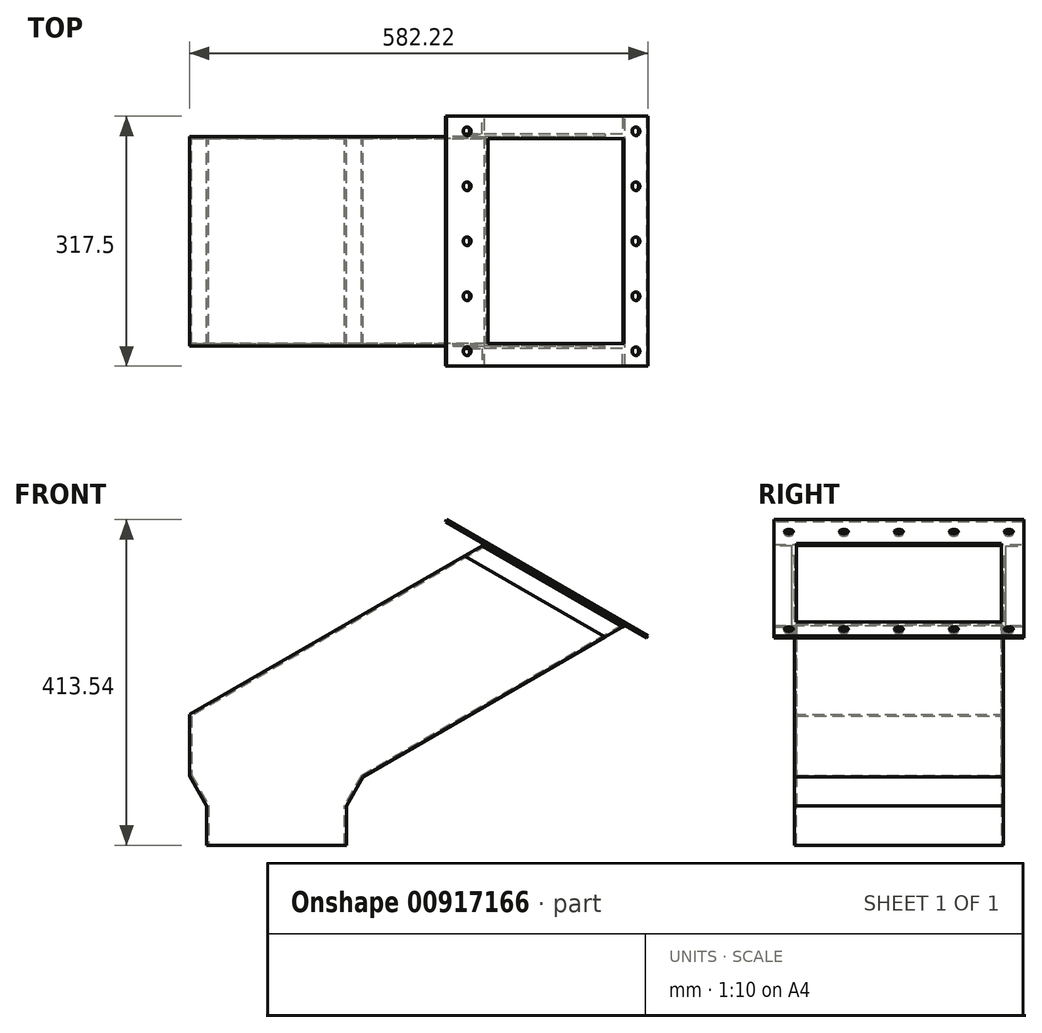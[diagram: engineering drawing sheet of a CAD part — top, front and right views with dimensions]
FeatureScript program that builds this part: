
annotation { "Feature Type Name" : "Feature", "Feature Type Description" : "" }
export const myFeature = defineFeature(function(context is Context, id is Id, definition is map)
    precondition{}
    {
        {
            var Q0;
            Q0=qCreatedBy(makeId("Front.planeOp"),FACE);
            var sketch = newSketch(context, id + "F0", { "sketchPlane" : qUnion([Q0])});
            skLineSegment(sketch, "E0", {"start": v(-317.85, 2733.04) * mm, "end": v(355.25, 2344.43) * mm});
            skLineSegment(sketch, "E1", {"start": v(355.25, 2344.43) * mm, "end": v(1028.35, 2733.04) * mm});
            skLineSegment(sketch, "E2", {"start": v(-317.85, 2733.04) * mm, "end": v(-317.85, 4597.4) * mm});
            skLineSegment(sketch, "E3", {"start": v(-317.85, 4597.4) * mm, "end": v(1028.35, 4597.4) * mm});
            skLineSegment(sketch, "E4", {"start": v(1028.35, 2733.04) * mm, "end": v(1028.35, 4597.4) * mm});
            skLineSegment(sketch, "E5", {"start": v(-317.85, 2733.04) * mm, "end": v(1028.35, 2733.04) * mm, "construction": true});
            skLineSegment(sketch, "E6", {"start": v(-317.85, 2739.4) * mm, "end": v(-368.65, 2739.4) * mm});
            skLineSegment(sketch, "E7", {"start": v(-368.65, 2733.04) * mm, "end": v(-368.65, 2739.4) * mm});
            skLineSegment(sketch, "E8", {"start": v(-368.65, 2733.04) * mm, "end": v(1079.15, 2733.04) * mm});
            skLineSegment(sketch, "E9", {"start": v(1079.15, 2739.4) * mm, "end": v(1079.15, 2733.04) * mm});
            skLineSegment(sketch, "E10", {"start": v(1079.15, 2739.4) * mm, "end": v(1028.35, 2739.4) * mm});
            skLineSegment(sketch, "E11", {"start": v(355.25, 4597.4) * mm, "end": v(355.25, 2344.43) * mm, "construction": true});
            skLineSegment(sketch, "E12", {"start": v(355.25, 2344.43) * mm, "end": v(0, 2139.33) * mm, "construction": true});
            skLineSegment(sketch, "E13", {"start": v(0, 2088) * mm, "end": v(0, 0) * mm, "construction": true});
            skLineSegment(sketch, "E14", {"start": v(-1118.25, 0) * mm, "end": v(0, 0) * mm, "construction": true});
            skLineSegment(sketch, "E15", {"start": v(-317.85, 2739.4) * mm, "end": v(-317.85, 2088) * mm, "construction": true});
            skLineSegment(sketch, "E16", {"start": v(-317.85, 2088) * mm, "end": v(-88.9, 2088) * mm, "construction": true});
            skLineSegment(sketch, "E17", {"start": v(-88.9, 2088) * mm, "end": v(0, 2088) * mm, "construction": true});
            skLineSegment(sketch, "E18", {"start": v(0, 2088) * mm, "end": v(0, 2139.33) * mm, "construction": true});
            skLineSegment(sketch, "E19", {"start": v(0, 2088) * mm, "end": v(0, 2088) * mm});
            skSolve(sketch);
        }
        {
            var Q0;
            Q0=qCreatedBy(makeId("Right.planeOp"),FACE);
            var sketch = newSketch(context, id + "F1", { "sketchPlane" : qUnion([Q0])});
            skLineSegment(sketch, "E20", {"start": v(0, 2549.53) * mm, "end": v(-535.95, 2549.53) * mm});
            skSolve(sketch);
        }
        {
            var Q0;
            Q0=sQuery(id+"F1.wireOp",VERTEX,"E20.end");
            var Q1;
            Q1=sQuery(id+"F0.wireOp",VERTEX,"E0.start");
            var Q2;
            Q2=sQuery(id+"F0.wireOp",VERTEX,"E0.end");
            cPlane(context, id + "F2", {"entities" : qUnion([Q0, Q1, Q2]), "cplaneType" : CPlaneType.THREE_POINT, "offset" : 3.17 * mm, "oppositeDirection" : true, "width" : 152.4 * mm, "height" : 152.4 * mm});
        }
        {
            var Q0;
            Q0=qCreatedBy(id+"F2.planeOp",FACE);
            var sketch = newSketch(context, id + "F3", { "sketchPlane" : qUnion([Q0])});
            skLineSegment(sketch, "E21.bottom", {"start": v(-1067.66, -130.18) * mm, "end": v(-1067.66, 130.17) * mm});
            skLineSegment(sketch, "E21.top", {"start": v(-867.64, -130.18) * mm, "end": v(-867.64, 130.17) * mm});
            skLineSegment(sketch, "E21.left", {"start": v(-1067.66, 130.17) * mm, "end": v(-867.64, 130.17) * mm});
            skLineSegment(sketch, "E21.right", {"start": v(-1067.66, -130.18) * mm, "end": v(-867.64, -130.18) * mm});
            skLineSegment(sketch, "E22.bottom", {"start": v(-1127.99, 158.75) * mm, "end": v(-832.71, 158.75) * mm});
            skLineSegment(sketch, "E22.top", {"start": v(-1127.99, -158.75) * mm, "end": v(-832.71, -158.75) * mm});
            skLineSegment(sketch, "E22.left", {"start": v(-1127.99, 158.75) * mm, "end": v(-1127.99, -158.75) * mm});
            skLineSegment(sketch, "E22.right", {"start": v(-832.71, 158.75) * mm, "end": v(-832.71, -158.75) * mm});
            skLineSegment(sketch, "E23", {"start": v(-967.65, 130.17) * mm, "end": v(-967.65, 158.75) * mm, "construction": true});
            skLineSegment(sketch, "E24", {"start": v(-832.71, 0) * mm, "end": v(-867.64, 0) * mm, "construction": true});
            skSolve(sketch);
        }
        {
            var Q0;
            Q0=qSketchRegion(id+"F3",true);
            extrude(context, id + "F4", {"entities" : qUnion([Q0]), "oppositeDirection" : true, "depth" : 3.17 * mm, "offsetDistance" : 25.4 * mm});
        }
        {
            var Q0;
            Q0=qCreatedBy(makeId("Front.planeOp"),FACE);
            var sketch = newSketch(context, id + "F5", { "sketchPlane" : qUnion([Q0])});
            skLineSegment(sketch, "E25", {"start": v(-175.13, 2062.6) * mm, "end": v(-2.67, 2062.6) * mm});
            skLineSegment(sketch, "E26", {"start": v(-2.67, 2062.6) * mm, "end": v(-2.67, 2113.4) * mm});
            skLineSegment(sketch, "E27", {"start": v(18.93, 2151.5) * mm, "end": v(-2.67, 2113.4) * mm});
            skLineSegment(sketch, "E28", {"start": v(18.93, 2151.5) * mm, "end": v(351, 2343.22) * mm});
            skLineSegment(sketch, "E29", {"start": v(351, 2343.22) * mm, "end": v(177.77, 2443.23) * mm});
            skLineSegment(sketch, "E30", {"start": v(177.77, 2443.23) * mm, "end": v(-196.73, 2227.02) * mm});
            skLineSegment(sketch, "E31", {"start": v(-196.73, 2227.02) * mm, "end": v(-196.73, 2151.5) * mm});
            skLineSegment(sketch, "E32", {"start": v(-196.73, 2151.5) * mm, "end": v(-175.13, 2113.4) * mm});
            skLineSegment(sketch, "E33", {"start": v(-175.13, 2113.4) * mm, "end": v(-175.13, 2062.6) * mm});
            skLineSegment(sketch, "E34", {"start": v(-88.9, 2062.6) * mm, "end": v(-88.9, 2189.26) * mm, "construction": true});
            skPoint(sketch, "E34.endSnap0", {"position": v(351, 2343.22) * mm});
            skLineSegment(sketch, "E35", {"start": v(-88.9, 2189.26) * mm, "end": v(264.38, 2393.23) * mm, "construction": true});
            skLineSegment(sketch, "E36", {"start": v(-88.9, 2088) * mm, "end": v(-88.9, 2062.6) * mm, "construction": true});
            skSolve(sketch);
        }
        {
            var Q0;
            Q0=qSketchRegion(id+"F5",true);
            extrude(context, id + "F6", {"entities" : qUnion([Q0]), "endBound" : BoundingType.SYMMETRIC, "depth" : 260.35 * mm, "offsetDistance" : 25.4 * mm});
        }
        {
            var Q0;
            Q0=makeQuery(id+"F6.opExtrude","SWEPT_FACE",FACE,{"disambiguationData":[OSD([sQuery(id+"F5.wireOp",EDGE,"E29")])]});
            var Q1;
            Q1=makeQuery(id+"F6.opExtrude","SWEPT_FACE",FACE,{"disambiguationData":[OSD([sQuery(id+"F5.wireOp",EDGE,"E25")])]});
            shell(context, id + "F7", {"entities" : qUnion([Q0, Q1]), "thickness" : 2.67 * mm, "oppositeDirection" : true});
        }
        {
            var Q0;
            Q0=sQuery(id+"F0.wireOp",VERTEX,"E0.end");
            var Q1;
            Q1=qCreatedBy(makeId("Right.planeOp"),FACE);
            cPlane(context, id + "F8", {"entities" : qUnion([Q0, Q1]), "cplaneType" : CPlaneType.PLANE_POINT, "offset" : 25.4 * mm, "width" : 152.4 * mm, "height" : 152.4 * mm});
        }
        {
            var Q0;
            Q0=qCreatedBy(id+"F8.planeOp",FACE);
            var sketch = newSketch(context, id + "F9", { "sketchPlane" : qUnion([Q0])});
            skLineSegment(sketch, "E37", {"start": v(0, 2344.43) * mm, "end": v(-111.8, 2344.43) * mm});
            skSolve(sketch);
        }
        {
            var Q0;
            Q0=sQuery(id+"F9.wireOp",EDGE,"E37");
            cPlane(context, id + "F10", {"entities" : qUnion([Q0]), "cplaneType" : CPlaneType.LINE_ANGLE, "offset" : 25.4 * mm, "angle" : 60 * degree, "width" : 152.4 * mm, "height" : 152.4 * mm});
        }
        {
            var Q0;
            Q0=qCreatedBy(id+"F10.planeOp",FACE);
            var Q1;
            Q1=sQuery(id+"F5.wireOp",VERTEX,"E35.end");
            cPlane(context, id + "F11", {"entities" : qUnion([Q0, Q1]), "cplaneType" : CPlaneType.PLANE_POINT, "offset" : 25.4 * mm, "width" : 152.4 * mm, "height" : 152.4 * mm});
        }
        {
            var Q0;
            Q0=qCreatedBy(id+"F11.planeOp",FACE);
            var sketch = newSketch(context, id + "F12", { "sketchPlane" : qUnion([Q0])});
            skLineSegment(sketch, "E38", {"start": v(-132.84, 2204.79) * mm, "end": v(-132.84, 2179.39) * mm});
            skLineSegment(sketch, "E39", {"start": v(-132.84, 2179.39) * mm, "end": v(-136.02, 2179.39) * mm});
            skLineSegment(sketch, "E40", {"start": v(-136.02, 2179.39) * mm, "end": v(-136.02, 2201.61) * mm});
            skLineSegment(sketch, "E41", {"start": v(-136.02, 2201.61) * mm, "end": v(-158.24, 2201.61) * mm});
            skLineSegment(sketch, "E42", {"start": v(-158.24, 2201.61) * mm, "end": v(-158.24, 2204.79) * mm});
            skLineSegment(sketch, "E43", {"start": v(-158.24, 2204.79) * mm, "end": v(-132.84, 2204.79) * mm});
            skLineSegment(sketch, "E44", {"start": v(0, 2204.79) * mm, "end": v(0, 2243.29) * mm, "construction": true});
            skLineSegment(sketch, "E45.MirrorCS", {"start": v(158.24, 2201.61) * mm, "end": v(158.24, 2204.79) * mm});
            skLineSegment(sketch, "E46.MirrorCS", {"start": v(132.84, 2179.39) * mm, "end": v(136.02, 2179.39) * mm});
            skLineSegment(sketch, "E47.MirrorCS", {"start": v(158.24, 2204.79) * mm, "end": v(132.84, 2204.79) * mm});
            skLineSegment(sketch, "E48.MirrorCS", {"start": v(136.02, 2179.39) * mm, "end": v(136.02, 2201.61) * mm});
            skLineSegment(sketch, "E49.MirrorCS", {"start": v(132.84, 2204.79) * mm, "end": v(132.84, 2179.39) * mm});
            skLineSegment(sketch, "E50.MirrorCS", {"start": v(136.02, 2201.61) * mm, "end": v(158.24, 2201.61) * mm});
            skSolve(sketch);
        }
        {
            var Q0;
            Q0 = qSketchRegion(id + "F12", true);
            var Q1;
            Q1=makeQuery(id+"F6.opExtrude","SWEPT_FACE",FACE,{"disambiguationData":[OSD([sQuery(id+"F5.wireOp",EDGE,"E28")])]});
            var Q2;
            Q2=makeQuery(id+"F6.opExtrude","SWEPT_FACE",FACE,{"disambiguationData":[OSD([sQuery(id+"F5.wireOp",EDGE,"E30")])]});
            extrude(context, id + "F13", {"entities" : qUnion([Q0]), "operationType" : NewBodyOperationType.ADD, "endBound" : BoundingType.UP_TO_SURFACE, "depth" : 25.4 * mm, "endBoundEntityFace" : qUnion([Q1]), "offsetDistance" : 25.4 * mm, "hasSecondDirection" : true, "secondDirectionBound" : SecondDirectionBoundingType.UP_TO_SURFACE, "secondDirectionOppositeDirection" : true, "secondDirectionDepth" : 25.4 * mm, "secondDirectionBoundEntityFace" : qUnion([Q2])});
        }
        {
            var Q0;
            Q0=makeQuery(id+"F4.opExtrude","CAP_FACE",FACE,{"disambiguationData":[OSD([sQuery(id+"F3.wireOp",EDGE,"E21.bottom"),sQuery(id+"F3.wireOp",EDGE,"E21.top"),sQuery(id+"F3.wireOp",EDGE,"E21.left"),sQuery(id+"F3.wireOp",EDGE,"E21.right"),sQuery(id+"F3.wireOp",EDGE,"E22.bottom"),sQuery(id+"F3.wireOp",EDGE,"E22.top"),sQuery(id+"F3.wireOp",EDGE,"E22.left"),sQuery(id+"F3.wireOp",EDGE,"E22.right")])],"isStart":true});
            var sketch = newSketch(context, id + "F14", { "sketchPlane" : qUnion([Q0])});
            skCircle(sketch, "E51", {"center": v(-850.18, -139.7) * mm, "radius": 5.56 * mm});
            skCircle(sketch, "E52", {"center": v(-1097.83, -139.7) * mm, "radius": 5.56 * mm});
            skLineSegment(sketch, "E53", {"start": v(-867.64, -139.7) * mm, "end": v(-850.18, -139.7) * mm, "construction": true});
            skLineSegment(sketch, "E54", {"start": v(-832.71, -139.7) * mm, "end": v(-850.18, -139.7) * mm, "construction": true});
            skCircle(sketch, "E55.0.1.0", {"center": v(-1097.83, -69.85) * mm, "radius": 5.56 * mm});
            skCircle(sketch, "E55.0.1.1", {"center": v(-850.18, -69.85) * mm, "radius": 5.56 * mm});
            skCircle(sketch, "E55.0.2.0", {"center": v(-1097.83, 0) * mm, "radius": 5.56 * mm});
            skCircle(sketch, "E55.0.2.1", {"center": v(-850.18, 0) * mm, "radius": 5.56 * mm});
            skCircle(sketch, "E55.0.3.0", {"center": v(-1097.83, 69.85) * mm, "radius": 5.56 * mm});
            skCircle(sketch, "E55.0.3.1", {"center": v(-850.18, 69.85) * mm, "radius": 5.56 * mm});
            skCircle(sketch, "E55.0.4.0", {"center": v(-1097.83, 139.7) * mm, "radius": 5.56 * mm});
            skCircle(sketch, "E55.0.4.1", {"center": v(-850.18, 139.7) * mm, "radius": 5.56 * mm});
            skLineSegment(sketch, "E55.direction1", {"start": v(-1097.83, -139.7) * mm, "end": v(-1067.66, -139.7) * mm, "construction": true});
            skLineSegment(sketch, "E55.direction2", {"start": v(-1097.83, -139.7) * mm, "end": v(-1097.83, -69.85) * mm, "construction": true});
            skLineSegment(sketch, "E56", {"start": v(-850.18, 158.75) * mm, "end": v(-850.18, -139.7) * mm, "construction": true});
            skLineSegment(sketch, "E57", {"start": v(-850.18, -158.75) * mm, "end": v(-850.18, 139.7) * mm, "construction": true});
            skLineSegment(sketch, "E58", {"start": v(-1097.83, -139.7) * mm, "end": v(-1127.99, -139.7) * mm, "construction": true});
            skSolve(sketch);
        }
        {
            var Q0;
            Q0 = qSketchRegion(id + "F14", true);
            extrude(context, id + "F15", {"entities" : qUnion([Q0]), "operationType" : NewBodyOperationType.REMOVE, "endBound" : BoundingType.UP_TO_NEXT, "oppositeDirection" : true, "depth" : 25.4 * mm, "offsetDistance" : 25.4 * mm});
        }
    });
